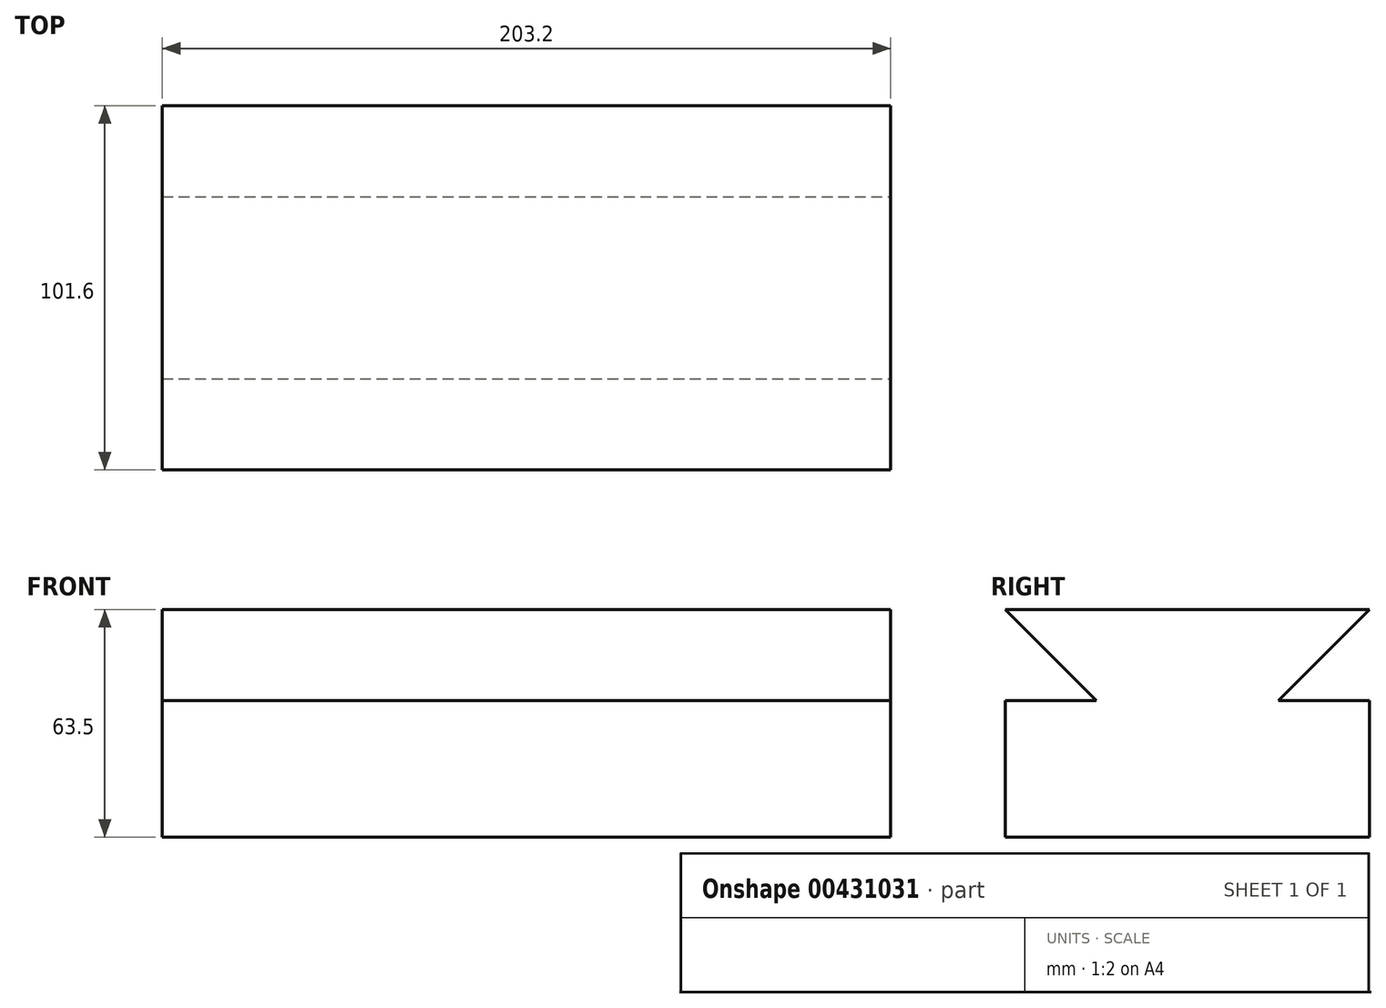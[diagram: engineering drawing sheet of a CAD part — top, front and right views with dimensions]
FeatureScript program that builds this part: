
annotation { "Feature Type Name" : "Feature", "Feature Type Description" : "" }
export const myFeature = defineFeature(function(context is Context, id is Id, definition is map)
    precondition{}
    {
        {
            var Q0;
            Q0=qCreatedBy(makeId("Right.planeOp"),FACE);
            var sketch = newSketch(context, id + "F0", { "sketchPlane" : qUnion([Q0])});
            skLineSegment(sketch, "E0.bottom", {"start": v(0, 0) * mm, "end": v(-101.6, 0) * mm});
            skLineSegment(sketch, "E0.top", {"start": v(0, 38.1) * mm, "end": v(-101.6, 38.1) * mm});
            skLineSegment(sketch, "E0.left", {"start": v(0, 0) * mm, "end": v(0, 38.1) * mm});
            skLineSegment(sketch, "E0.right", {"start": v(-101.6, 0) * mm, "end": v(-101.6, 38.1) * mm});
            skLineSegment(sketch, "E1", {"start": v(-101.6, 63.5) * mm, "end": v(0, 63.5) * mm});
            skLineSegment(sketch, "E2", {"start": v(0, 63.5) * mm, "end": v(-25.4, 38.1) * mm});
            skLineSegment(sketch, "E3", {"start": v(-25.4, 38.1) * mm, "end": v(-76.2, 38.1) * mm});
            skLineSegment(sketch, "E4", {"start": v(-76.2, 38.1) * mm, "end": v(-101.6, 63.5) * mm});
            skSolve(sketch);
        }
        {
            var Q0;
            Q0=qCreatedBy(makeId("Top.planeOp"),FACE);
            var sketch = newSketch(context, id + "F1", { "sketchPlane" : qUnion([Q0])});
            skLineSegment(sketch, "E5.bottom", {"start": v(-203.2, 0) * mm, "end": v(0, 0) * mm});
            skLineSegment(sketch, "E5.top", {"start": v(-203.2, -101.6) * mm, "end": v(0, -101.6) * mm});
            skLineSegment(sketch, "E5.left", {"start": v(-203.2, 0) * mm, "end": v(-203.2, -101.6) * mm});
            skLineSegment(sketch, "E5.right", {"start": v(0, 0) * mm, "end": v(0, -101.6) * mm});
            skSolve(sketch);
        }
        {
            var Q0;
            Q0=makeQuery(id+"F1.imprint","IMPRINT",FACE,{"disambiguationData":[TD([[makeQuery(id+"F1.imprint","IMPRINT",EDGE,{"derivedFrom":sQuery(id+"F1.wireOp",EDGE,"E5.bottom")}),-1.0]])]});
            extrude(context, id + "F2", {"entities" : qUnion([Q0]), "depth" : 38.1 * mm});
        }
        {
            var Q0;
            Q0=makeQuery(id+"F0.imprint","IMPRINT",FACE,{"disambiguationData":[TD([[makeQuery(id+"F0.imprint","IMPRINT",EDGE,{"derivedFrom":sQuery(id+"F0.wireOp",EDGE,"E1")}),-1.0]])]});
            extrude(context, id + "F3", {"entities" : qUnion([Q0]), "operationType" : NewBodyOperationType.ADD, "oppositeDirection" : true, "depth" : 203.2 * mm});
        }
    });
